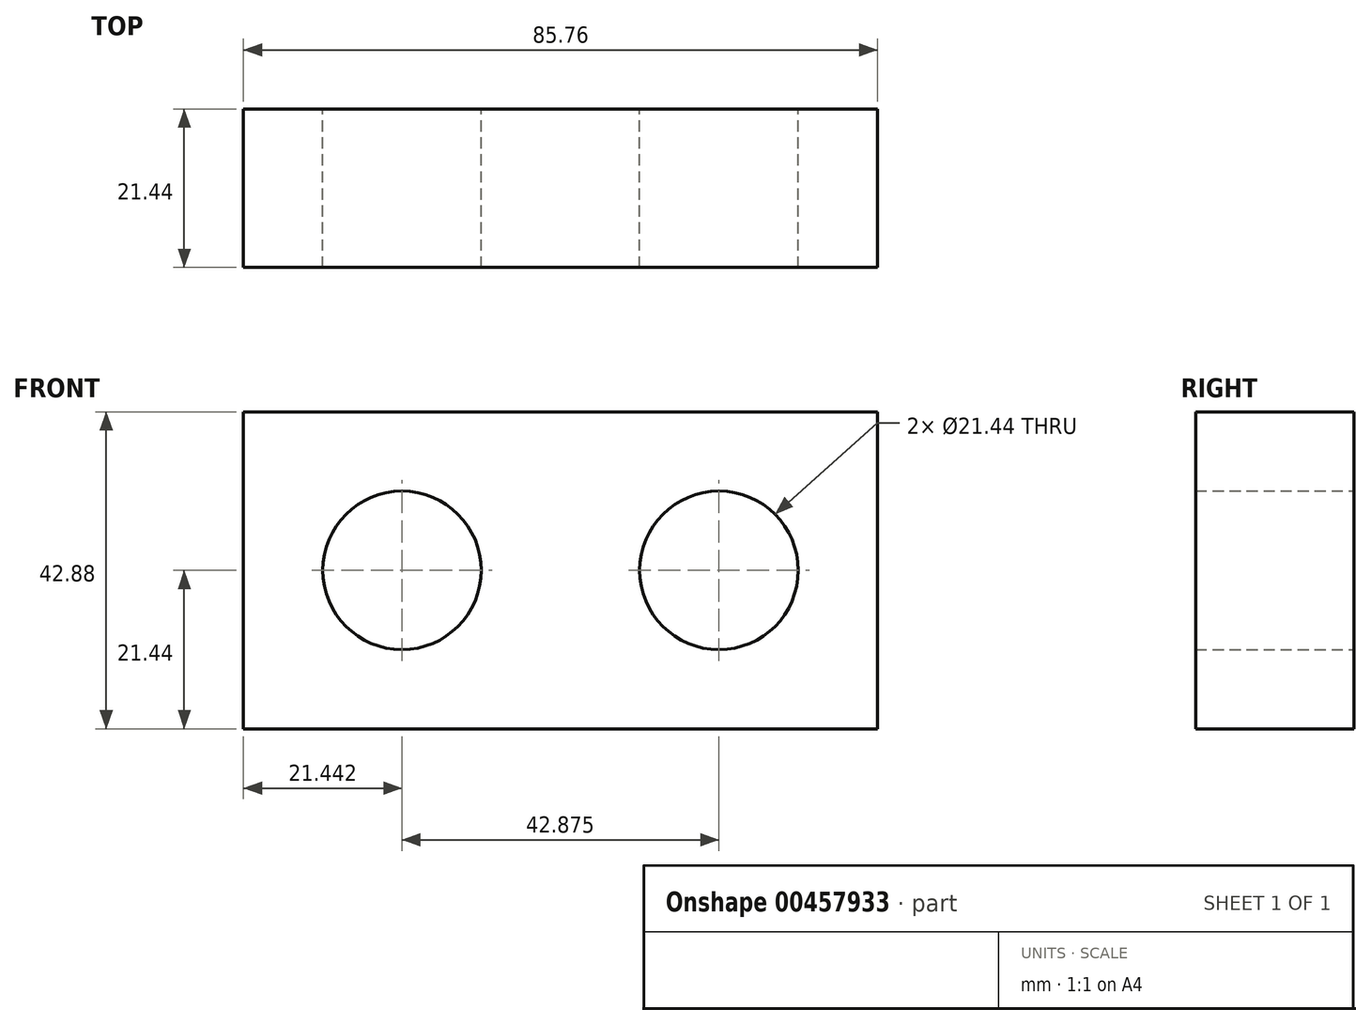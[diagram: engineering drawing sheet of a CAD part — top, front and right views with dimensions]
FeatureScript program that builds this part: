
annotation { "Feature Type Name" : "Feature", "Feature Type Description" : "" }
export const myFeature = defineFeature(function(context is Context, id is Id, definition is map)
    precondition{}
    {
        {
            var Q0;
            Q0=qCreatedBy(makeId("Front.planeOp"),FACE);
            var sketch = newSketch(context, id + "F0", { "sketchPlane" : qUnion([Q0])});
            skLineSegment(sketch, "E0.bottom", {"start": v(0, 21.44) * mm, "end": v(42.88, 21.44) * mm});
            skLineSegment(sketch, "E0.top", {"start": v(0, -21.44) * mm, "end": v(42.88, -21.44) * mm});
            skLineSegment(sketch, "E0.left", {"start": v(0, 21.44) * mm, "end": v(0, -21.44) * mm});
            skLineSegment(sketch, "E0.right", {"start": v(42.88, 21.44) * mm, "end": v(42.88, -21.44) * mm});
            skPoint(sketch, "E0.middle", {"position": v(21.44, 0) * mm});
            skCircle(sketch, "E1", {"center": v(21.44, 0) * mm, "radius": 10.72 * mm});
            skCircle(sketch, "E2.MirrorC", {"center": v(-21.44, 0) * mm, "radius": 10.72 * mm});
            skLineSegment(sketch, "E3.MirrorCS", {"start": v(-42.88, 21.44) * mm, "end": v(-42.88, -21.44) * mm});
            skLineSegment(sketch, "E4.MirrorCS", {"start": v(0, -21.44) * mm, "end": v(-42.88, -21.44) * mm});
            skLineSegment(sketch, "E5.MirrorCS", {"start": v(0, 21.44) * mm, "end": v(-42.88, 21.44) * mm});
            skSolve(sketch);
        }
        {
            var Q0;
            Q0 = qSketchRegion(id + "F0", true);
            extrude(context, id + "F1", {"entities" : qUnion([Q0]), "depth" : 21.44 * mm, "offsetDistance" : 25.4 * mm});
        }
    });
